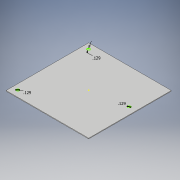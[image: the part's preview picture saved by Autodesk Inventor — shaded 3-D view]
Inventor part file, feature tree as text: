
AUTODESK INVENTOR PART (.ipt)
format: ipt  version: 2018 (Build 220112000, 112)  size: 96,768 bytes
history: native  units: in
note: dims shown in document units (in); Inventor stores cm internally (conversion verified against a paired STEP export)
features: sketch x2, extrude x1
ambient origin geometry x8: Origin, YZ Plane, XZ Plane, XY Plane, X Axis, Y Axis, Z Axis, Center Point
bodies: Body1 (feature_tree)
feature tree (3):
  extrude  "Extrusion2"  Depth=3.937in
  sketch  "Sketch3"  dims[d6=0.031in d7=0.0in d8=0.1285in d9=0.1285in d10=0.1285in]
  sketch  "Sketch2"  dims[d4=3.937in d5=3.937in]
